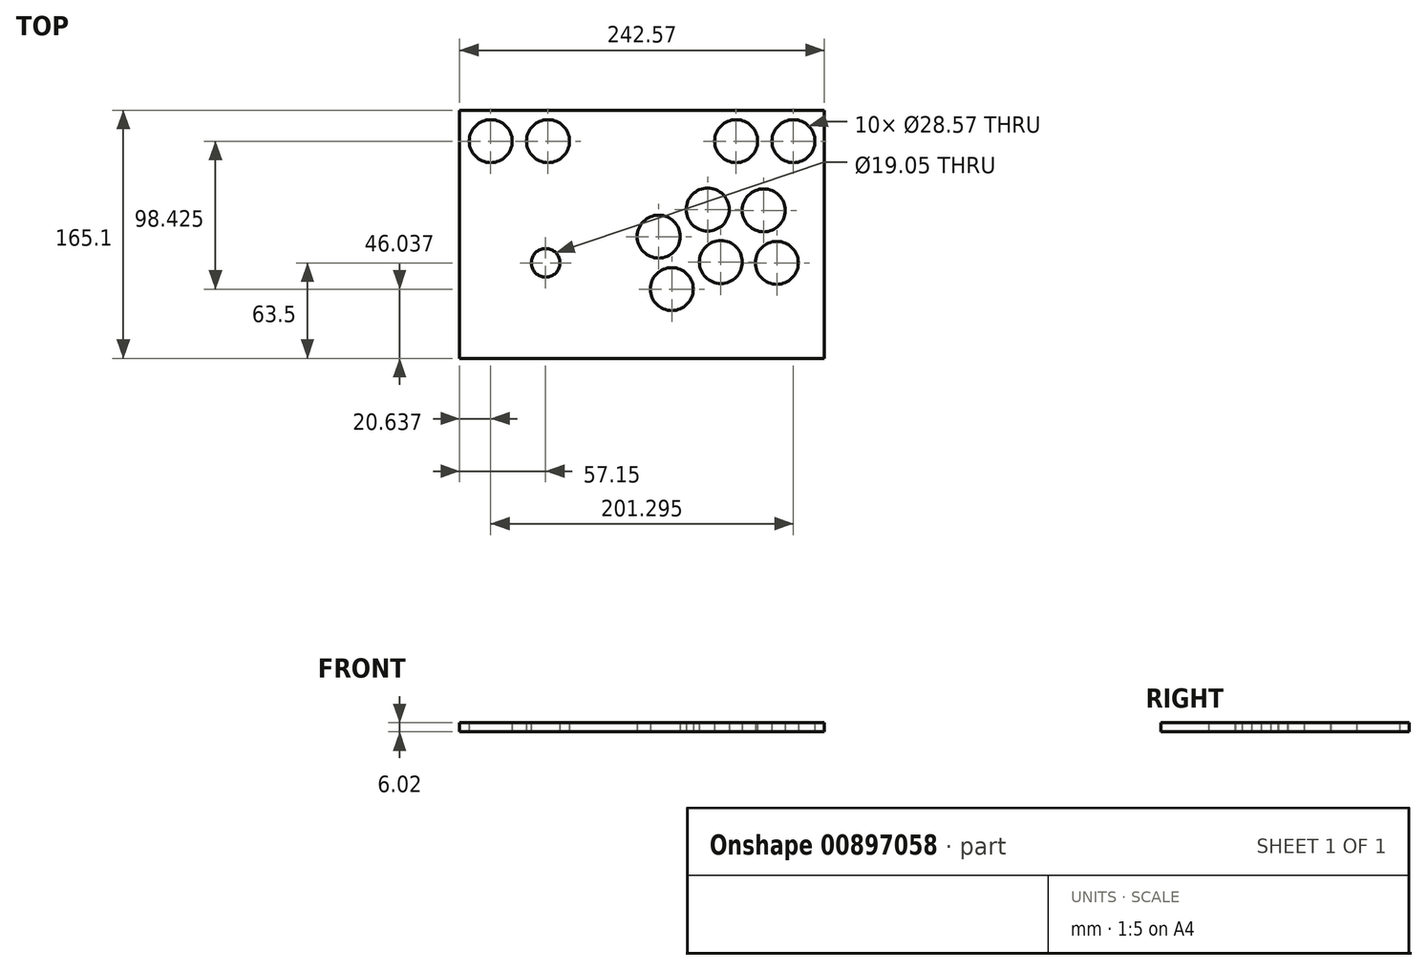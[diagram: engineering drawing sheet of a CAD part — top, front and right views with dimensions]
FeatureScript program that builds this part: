
annotation { "Feature Type Name" : "Feature", "Feature Type Description" : "" }
export const myFeature = defineFeature(function(context is Context, id is Id, definition is map)
    precondition{}
    {
        {
            var Q0;
            Q0=qCreatedBy(makeId("Top.planeOp"),FACE);
            var sketch = newSketch(context, id + "F0", { "sketchPlane" : qUnion([Q0])});
            skLineSegment(sketch, "E0.bottom", {"start": v(0, 0) * mm, "end": v(242.57, 0) * mm});
            skLineSegment(sketch, "E0.top", {"start": v(0, 165.1) * mm, "end": v(242.57, 165.1) * mm});
            skLineSegment(sketch, "E0.left", {"start": v(0, 0) * mm, "end": v(0, 165.1) * mm});
            skLineSegment(sketch, "E0.right", {"start": v(242.57, 0) * mm, "end": v(242.57, 165.1) * mm});
            skCircle(sketch, "E1", {"center": v(57.15, 63.5) * mm, "radius": 9.53 * mm});
            skCircle(sketch, "E2", {"center": v(132.3, 80.96) * mm, "radius": 14.29 * mm});
            skCircle(sketch, "E3", {"center": v(164.92, 98.93) * mm, "radius": 14.29 * mm});
            skCircle(sketch, "E4", {"center": v(202.15, 98.43) * mm, "radius": 14.29 * mm});
            skCircle(sketch, "E5", {"center": v(141.04, 46.04) * mm, "radius": 14.29 * mm});
            skCircle(sketch, "E6", {"center": v(173.65, 64) * mm, "radius": 14.29 * mm});
            skCircle(sketch, "E7", {"center": v(210.89, 63.5) * mm, "radius": 14.29 * mm});
            skCircle(sketch, "E8", {"center": v(20.64, 144.46) * mm, "radius": 14.29 * mm});
            skCircle(sketch, "E9", {"center": v(58.74, 144.46) * mm, "radius": 14.29 * mm});
            skLineSegment(sketch, "E10", {"start": v(202.15, 98.43) * mm, "end": v(132.3, 80.96) * mm, "construction": true});
            skLineSegment(sketch, "E11", {"start": v(132.3, 80.96) * mm, "end": v(141.04, 46.04) * mm, "construction": true});
            skLineSegment(sketch, "E12", {"start": v(202.15, 98.43) * mm, "end": v(210.89, 63.5) * mm, "construction": true});
            skLineSegment(sketch, "E13", {"start": v(210.89, 63.5) * mm, "end": v(141.04, 46.04) * mm, "construction": true});
            skPoint(sketch, "E14", {"position": v(167.23, 89.7) * mm});
            skPoint(sketch, "E15", {"position": v(175.96, 54.77) * mm});
            skLineSegment(sketch, "E16", {"start": v(175.96, 54.77) * mm, "end": v(164.92, 98.93) * mm, "construction": true});
            skPoint(sketch, "E17", {"position": v(121.29, 165.1) * mm});
            skPoint(sketch, "E18", {"position": v(121.29, 0) * mm});
            skLineSegment(sketch, "E19", {"start": v(121.29, 165.1) * mm, "end": v(121.29, 0) * mm, "construction": true});
            skCircle(sketch, "E20", {"center": v(183.83, 144.46) * mm, "radius": 14.29 * mm});
            skCircle(sketch, "E21", {"center": v(221.93, 144.46) * mm, "radius": 14.29 * mm});
            skLineSegment(sketch, "E22.bottom", {"start": v(24.7, 112) * mm, "end": v(89.6, 112) * mm, "construction": true});
            skLineSegment(sketch, "E22.top", {"start": v(24.7, 15) * mm, "end": v(89.6, 15) * mm, "construction": true});
            skLineSegment(sketch, "E22.left", {"start": v(24.7, 112) * mm, "end": v(24.7, 15) * mm, "construction": true});
            skLineSegment(sketch, "E22.right", {"start": v(89.6, 112) * mm, "end": v(89.6, 15) * mm, "construction": true});
            skPoint(sketch, "E23", {"position": v(57.15, 112) * mm});
            skPoint(sketch, "E24", {"position": v(57.15, 15) * mm});
            skLineSegment(sketch, "E25", {"start": v(57.15, 112) * mm, "end": v(57.15, 15) * mm, "construction": true});
            skPoint(sketch, "E26", {"position": v(136.67, 63.5) * mm});
            skCircle(sketch, "E27", {"center": v(20.64, 144.46) * mm, "radius": 17.5 * mm, "construction": true});
            skCircle(sketch, "E28", {"center": v(58.74, 144.46) * mm, "radius": 17.5 * mm, "construction": true});
            skCircle(sketch, "E29", {"center": v(183.83, 144.46) * mm, "radius": 17.5 * mm, "construction": true});
            skCircle(sketch, "E30", {"center": v(221.93, 144.46) * mm, "radius": 17.5 * mm, "construction": true});
            skCircle(sketch, "E31", {"center": v(202.15, 98.43) * mm, "radius": 17.5 * mm, "construction": true});
            skCircle(sketch, "E32", {"center": v(210.89, 63.5) * mm, "radius": 17.5 * mm, "construction": true});
            skCircle(sketch, "E33", {"center": v(164.92, 98.93) * mm, "radius": 17.5 * mm, "construction": true});
            skCircle(sketch, "E34", {"center": v(132.3, 80.96) * mm, "radius": 17.5 * mm, "construction": true});
            skCircle(sketch, "E35", {"center": v(141.04, 46.04) * mm, "radius": 17.5 * mm, "construction": true});
            skCircle(sketch, "E36", {"center": v(173.65, 64) * mm, "radius": 17.5 * mm, "construction": true});
            skSolve(sketch);
        }
        {
            var Q0;
            Q0 = qSketchRegion(id + "F0", true);
            extrude(context, id + "F1", {"entities" : qUnion([Q0]), "depth" : 6.02 * mm, "offsetDistance" : 25.4 * mm});
        }
    });
